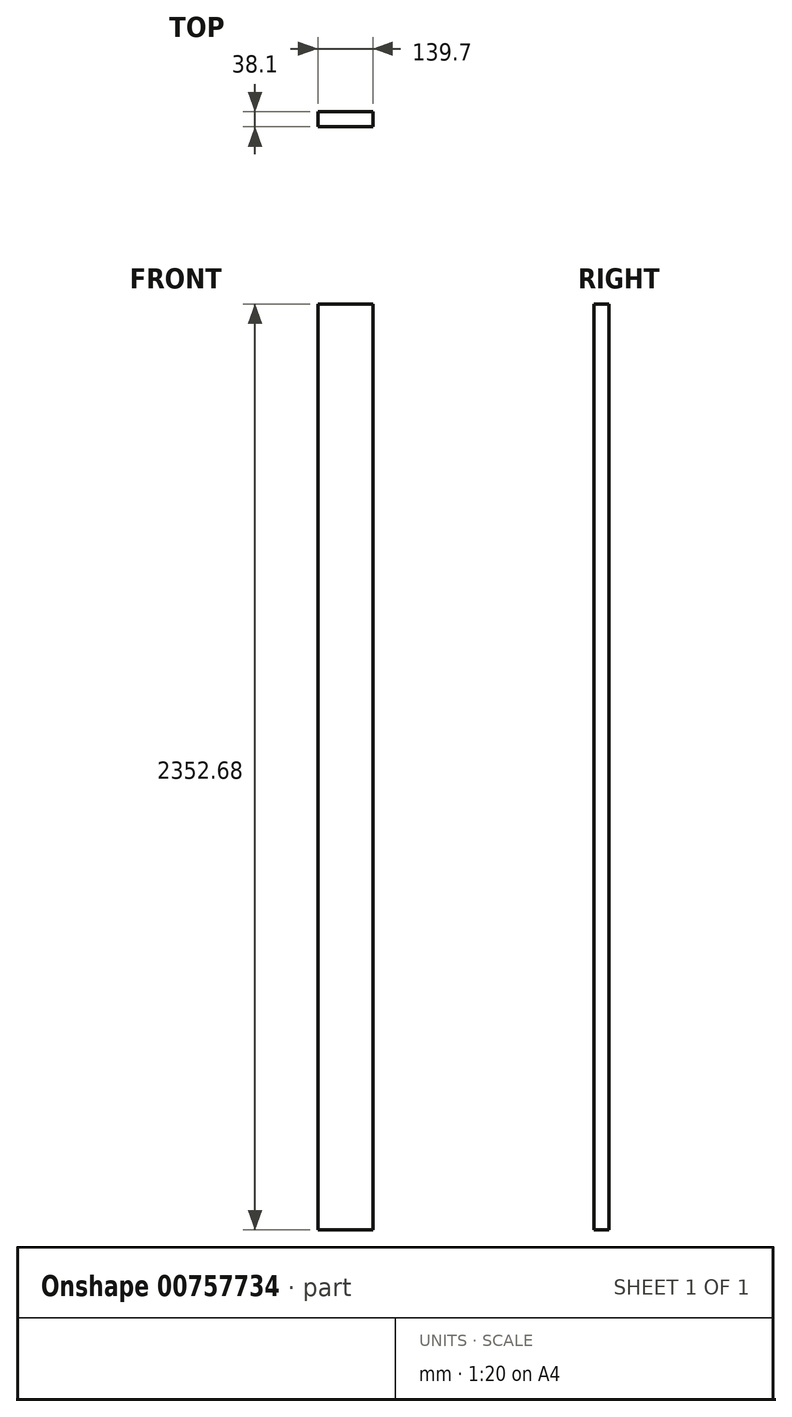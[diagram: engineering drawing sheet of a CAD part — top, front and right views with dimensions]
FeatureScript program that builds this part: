
annotation { "Feature Type Name" : "Feature", "Feature Type Description" : "" }
export const myFeature = defineFeature(function(context is Context, id is Id, definition is map)
    precondition{}
    {
        {
            var Q0;
            Q0=qCreatedBy(makeId("Top.planeOp"),FACE);
            var sketch = newSketch(context, id + "F0", { "sketchPlane" : qUnion([Q0])});
            skLineSegment(sketch, "E0.bottom", {"start": v(0, 0) * mm, "end": v(139.7, 0) * mm});
            skLineSegment(sketch, "E0.top", {"start": v(0, 38.1) * mm, "end": v(139.7, 38.1) * mm});
            skLineSegment(sketch, "E0.left", {"start": v(0, 0) * mm, "end": v(0, 38.1) * mm});
            skLineSegment(sketch, "E0.right", {"start": v(139.7, 0) * mm, "end": v(139.7, 38.1) * mm});
            skSolve(sketch);
        }
        {
            var Q0;
            Q0 = qSketchRegion(id + "F0", true);
            extrude(context, id + "F1", {"entities" : qUnion([Q0]), "depth" : 2352.67 * mm, "offsetDistance" : 25.4 * mm});
        }
    });
